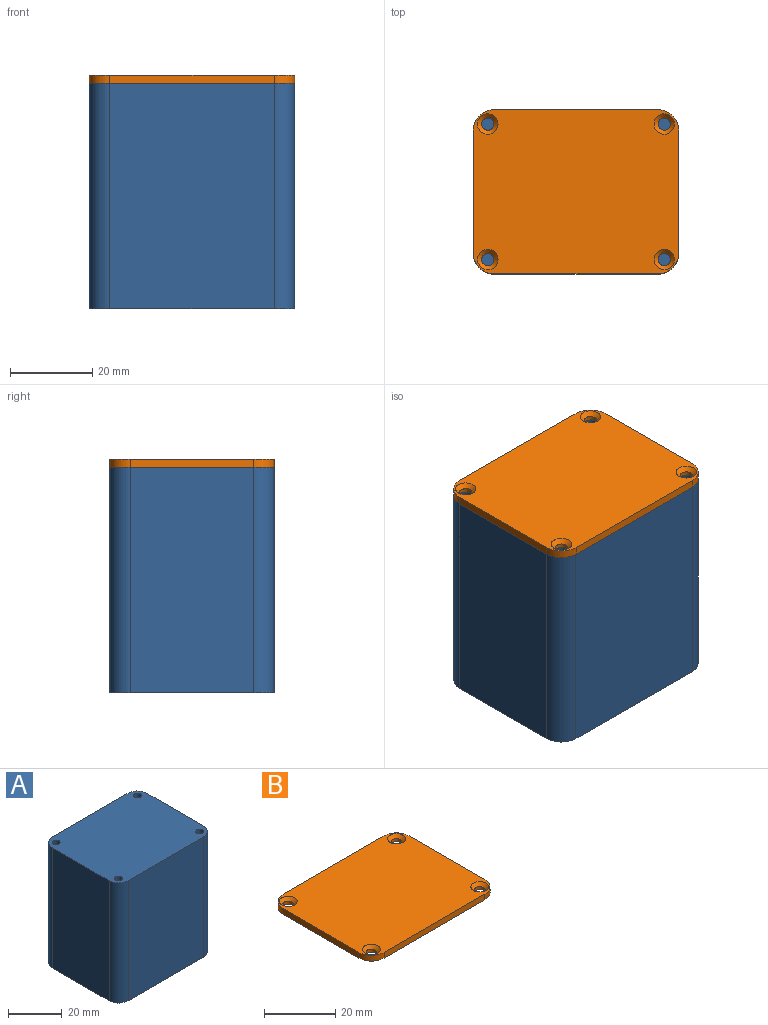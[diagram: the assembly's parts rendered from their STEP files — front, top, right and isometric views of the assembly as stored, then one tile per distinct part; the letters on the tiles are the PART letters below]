
ASSEMBLY  parts=2 mates=1
PART A: 18 faces, bbox 50x40x55 mm
  f0: plane 55x40mm, normal (0,1,0), area 2200mm2, adj f4,f5,f14,f17
  f1: plane 55x30mm, normal (-1,0,0), area 1650mm2, adj f4,f5,f14,f15
  f2: plane 55x40mm, normal (0,-1,0), area 2200mm2, adj f4,f5,f15,f16
  f3: plane 55x30mm, normal (1,0,0), area 1650mm2, adj f4,f5,f16,f17
  f4: plane 50x40mm, normal (0,0,1), area 1950.3mm2, adj f0,f1,f2,f3,f6,f8,f10,f12
  f5: plane 50x40mm, normal (0,0,-1), area 1978.5mm2, adj f0,f1,f2,f3,f14,f15,f16,f17
  f6: cylinder r=1.5mm len=25mm, axis (0,0,1), area 235.6mm2, adj f4,f7
  f7: plane 3x3mm, normal (0,0,1), area 7.1mm2, adj f6
  f8: cylinder r=1.5mm len=25mm, axis (0,0,1), area 235.6mm2, adj f4,f9
  f9: plane 3x3mm, normal (0,0,1), area 7.1mm2, adj f8
  f10: cylinder r=1.5mm len=25mm, axis (0,0,1), area 235.6mm2, adj f4,f11
  f11: plane 3x3mm, normal (0,0,1), area 7.1mm2, adj f10
  f12: cylinder r=1.5mm len=25mm, axis (0,0,1), area 235.6mm2, adj f4,f13
  f13: plane 3x3mm, normal (0,0,1), area 7.1mm2, adj f12
  f14: cylinder r=5mm len=55mm, axis (0,0,1), area 432mm2, adj f0,f1,f4,f5
  f15: cylinder r=5mm len=55mm, axis (0,0,-1), area 432mm2, adj f1,f2,f4,f5
  f16: cylinder r=5mm len=55mm, axis (0,0,1), area 432mm2, adj f2,f3,f4,f5
  f17: cylinder r=5mm len=55mm, axis (0,0,-1), area 432mm2, adj f0,f3,f4,f5
PART B: 18 faces, bbox 50x40x2 mm
  f0: plane 30x2mm, normal (-1,0,0), area 60mm2, adj f4,f5,f14,f17
  f1: plane 40x2mm, normal (0,-1,0), area 80mm2, adj f4,f5,f14,f15
  f2: plane 30x2mm, normal (1,0,0), area 60mm2, adj f4,f5,f15,f16
  f3: plane 40x2mm, normal (0,1,0), area 80mm2, adj f4,f5,f16,f17
  f4: plane 50x40mm, normal (0,0,1), area 1900mm2, adj f0,f1,f2,f3,f10,f11,f12,f13
  f5: plane 50x40mm, normal (0,0,-1), area 1950.3mm2, adj f0,f1,f2,f3,f6,f7,f8,f9
  f6: cylinder r=1.5mm len=3mm, axis (0,0,1), area 9.4mm2, adj f5,f10
  f7: cylinder r=1.5mm len=3mm, axis (0,0,1), area 9.4mm2, adj f5,f13
  f8: cylinder r=1.5mm len=3mm, axis (0,0,1), area 9.4mm2, adj f5,f12
  f9: cylinder r=1.5mm len=3mm, axis (0,0,1), area 9.4mm2, adj f5,f11
  f10: cone r=1.5mm half-angle=45deg, axis (0,0,1), area 17.8mm2, adj f4,f6
  f11: cone r=1.5mm half-angle=45deg, axis (0,0,1), area 17.8mm2, adj f4,f9
  f12: cone r=1.5mm half-angle=45deg, axis (0,0,1), area 17.8mm2, adj f4,f8
  f13: cone r=1.5mm half-angle=45deg, axis (0,0,1), area 17.8mm2, adj f4,f7
  f14: cylinder r=5mm len=5mm, axis (0,0,1), area 15.7mm2, adj f0,f1,f4,f5
  f15: cylinder r=5mm len=5mm, axis (0,0,-1), area 15.7mm2, adj f1,f2,f4,f5
  f16: cylinder r=5mm len=5mm, axis (0,0,1), area 15.7mm2, adj f2,f3,f4,f5
  f17: cylinder r=5mm len=5mm, axis (0,0,-1), area 15.7mm2, adj f0,f3,f4,f5
PLACE A t=(-72.15,-40.42,25.63)mm fixed
PLACE B t=(-144.6,-46.96,80.63)mm
MATE slider A.f10 <-> B.f9  axis (0,0,1) through (-84.86,-24.86,80.63)mm
